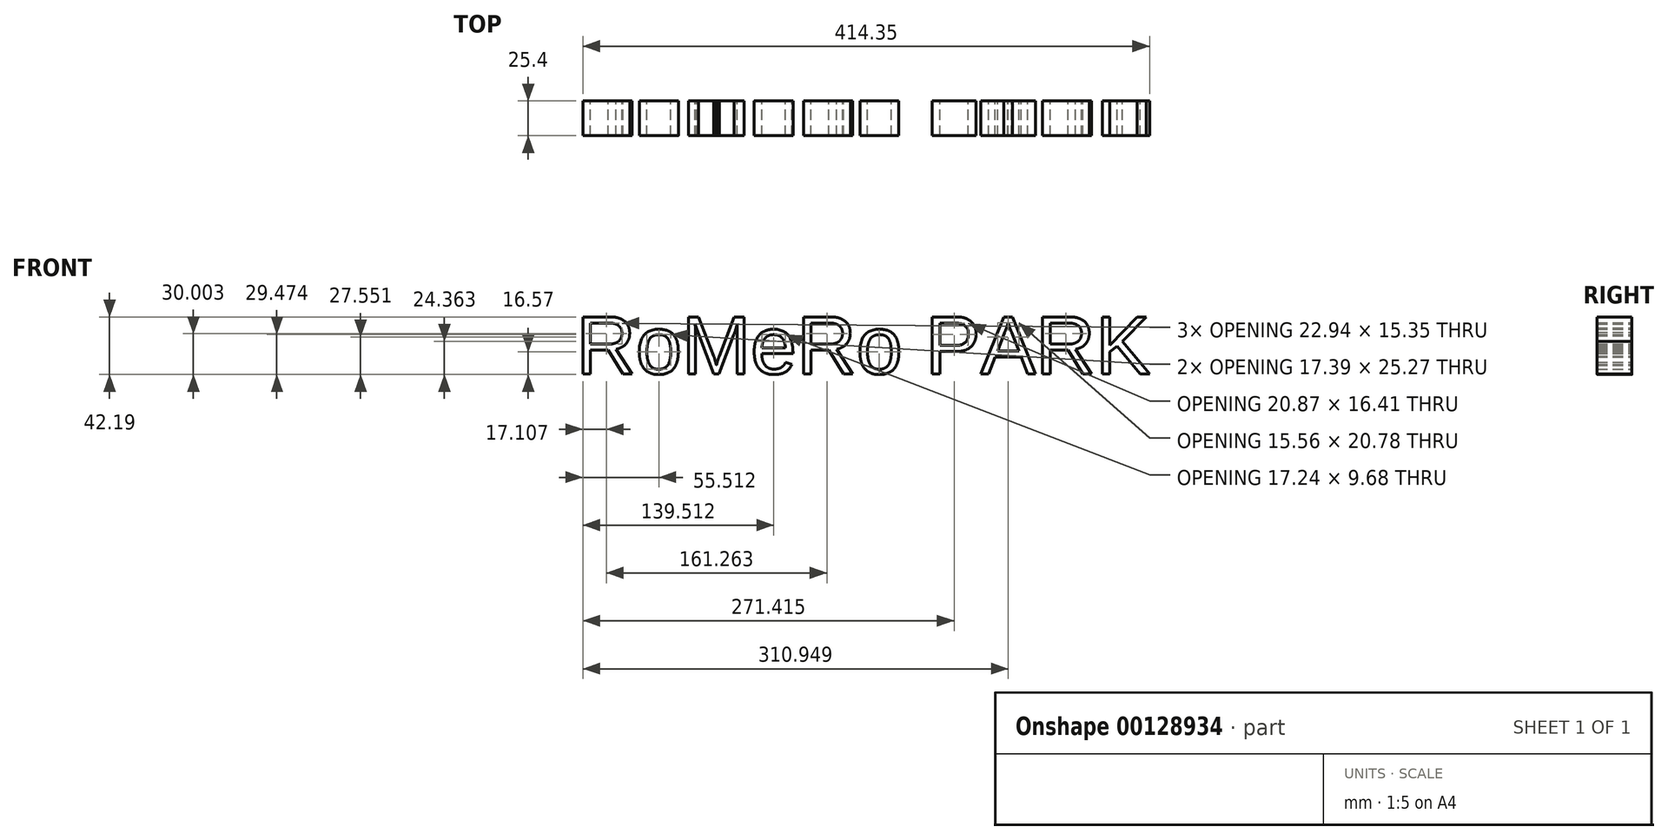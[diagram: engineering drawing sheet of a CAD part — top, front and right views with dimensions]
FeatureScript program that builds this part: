
annotation { "Feature Type Name" : "Feature", "Feature Type Description" : "" }
export const myFeature = defineFeature(function(context is Context, id is Id, definition is map)
    precondition{}
    {
        {
            var Q0;
            Q0=qCreatedBy(makeId("Front.planeOp"),FACE);
            var sketch = newSketch(context, id + "F0", { "sketchPlane" : qUnion([Q0])});
            skText(sketch, "E0", { "text": "RoMeRo PARK", "fontName": "Arimo-Regular.ttf"});
            const initialGuessF0  = {"E0": [-0.21177, 0, 1, 0, 0.04353]};
            skSetInitialGuess(sketch, initialGuessF0);
            skSolve(sketch);
        }
        {
            var Q0;
            Q0 = qSketchRegion(id + "F0", true);
            extrude(context, id + "F1", {"entities" : qUnion([Q0]), "endBound" : BoundingType.SYMMETRIC, "depth" : 25.4 * mm});
        }
        {
            var Q0;
            Q0=qCreatedBy(makeId("Front.planeOp"),FACE);
            var sketch = newSketch(context, id + "F2", { "sketchPlane" : qUnion([Q0])});
            skLineSegment(sketch, "E1.bottom", {"start": v(-239.46, 0) * mm, "end": v(-239.46, 0) * mm});
            skLineSegment(sketch, "E1.top", {"start": v(-239.46, 23.1) * mm, "end": v(-239.46, 23.1) * mm});
            skLineSegment(sketch, "E1.left", {"start": v(-239.46, 0) * mm, "end": v(-239.46, 12.8) * mm});
            skLineSegment(sketch, "E1.right", {"start": v(-239.46, 0) * mm, "end": v(-239.46, 12.8) * mm});
            skLineSegment(sketch, "E2.bottom", {"start": v(-229.02, 12.66) * mm, "end": v(-249.9, 12.66) * mm});
            skLineSegment(sketch, "E2.top", {"start": v(-229.02, 33.54) * mm, "end": v(-249.9, 33.54) * mm});
            skLineSegment(sketch, "E2.left", {"start": v(-229.02, 12.66) * mm, "end": v(-229.02, 33.54) * mm});
            skLineSegment(sketch, "E2.right", {"start": v(-249.9, 12.66) * mm, "end": v(-249.9, 33.54) * mm});
            skPoint(sketch, "E2.middle", {"position": v(-239.46, 23.1) * mm});
            skCircle(sketch, "E3", {"center": v(-239.46, 25.73) * mm, "radius": 12.92 * mm});
            skLineSegment(sketch, "E4.bottom", {"start": v(0, -17.7) * mm, "end": v(0, -17.7) * mm});
            skLineSegment(sketch, "E4.top", {"start": v(0, 5.4) * mm, "end": v(0, 5.4) * mm});
            skLineSegment(sketch, "E4.left", {"start": v(0, -17.7) * mm, "end": v(0, -5.04) * mm});
            skLineSegment(sketch, "E4.right", {"start": v(0, -17.7) * mm, "end": v(0, -5.04) * mm});
            skLineSegment(sketch, "E5.bottom", {"start": v(10.44, -5.04) * mm, "end": v(-10.44, -5.04) * mm});
            skLineSegment(sketch, "E5.top", {"start": v(10.44, 15.84) * mm, "end": v(-10.44, 15.84) * mm});
            skLineSegment(sketch, "E5.left", {"start": v(10.44, -5.04) * mm, "end": v(10.44, 15.84) * mm});
            skLineSegment(sketch, "E5.right", {"start": v(-10.44, -5.04) * mm, "end": v(-10.44, 15.84) * mm});
            skPoint(sketch, "E5.middle", {"position": v(0, 5.4) * mm});
            skCircle(sketch, "E6", {"center": v(0, 8.03) * mm, "radius": 13.07 * mm});
            skSolve(sketch);
        }
        {
            var Q0;
            Q0=sQuery(id+"F2.wireOp",EDGE,"E3");
            extrude(context, id + "F3", {"bodyType" : ToolBodyType.SURFACE, "surfaceEntities" : qUnion([Q0]), "endBound" : BoundingType.SYMMETRIC, "depth" : 6.35 * mm});
        }
        {
            var Q0;
            Q0=sQuery(id+"F2.wireOp",EDGE,"E2.top");
            var Q1;
            Q1=sQuery(id+"F2.wireOp",EDGE,"E2.right");
            var Q2;
            Q2=sQuery(id+"F2.wireOp",EDGE,"E2.left");
            var Q3;
            Q3=sQuery(id+"F2.wireOp",EDGE,"E2.bottom");
            extrude(context, id + "F4", {"bodyType" : ToolBodyType.SURFACE, "surfaceEntities" : qUnion([Q0, Q1, Q2, Q3]), "endBound" : BoundingType.SYMMETRIC, "depth" : 6.35 * mm});
        }
        {
            var Q0;
            Q0=sQuery(id+"F2.wireOp",EDGE,"E1.right");
            extrude(context, id + "F5", {"bodyType" : ToolBodyType.SURFACE, "surfaceEntities" : qUnion([Q0]), "endBound" : BoundingType.SYMMETRIC, "depth" : 6.35 * mm});
        }
    });
